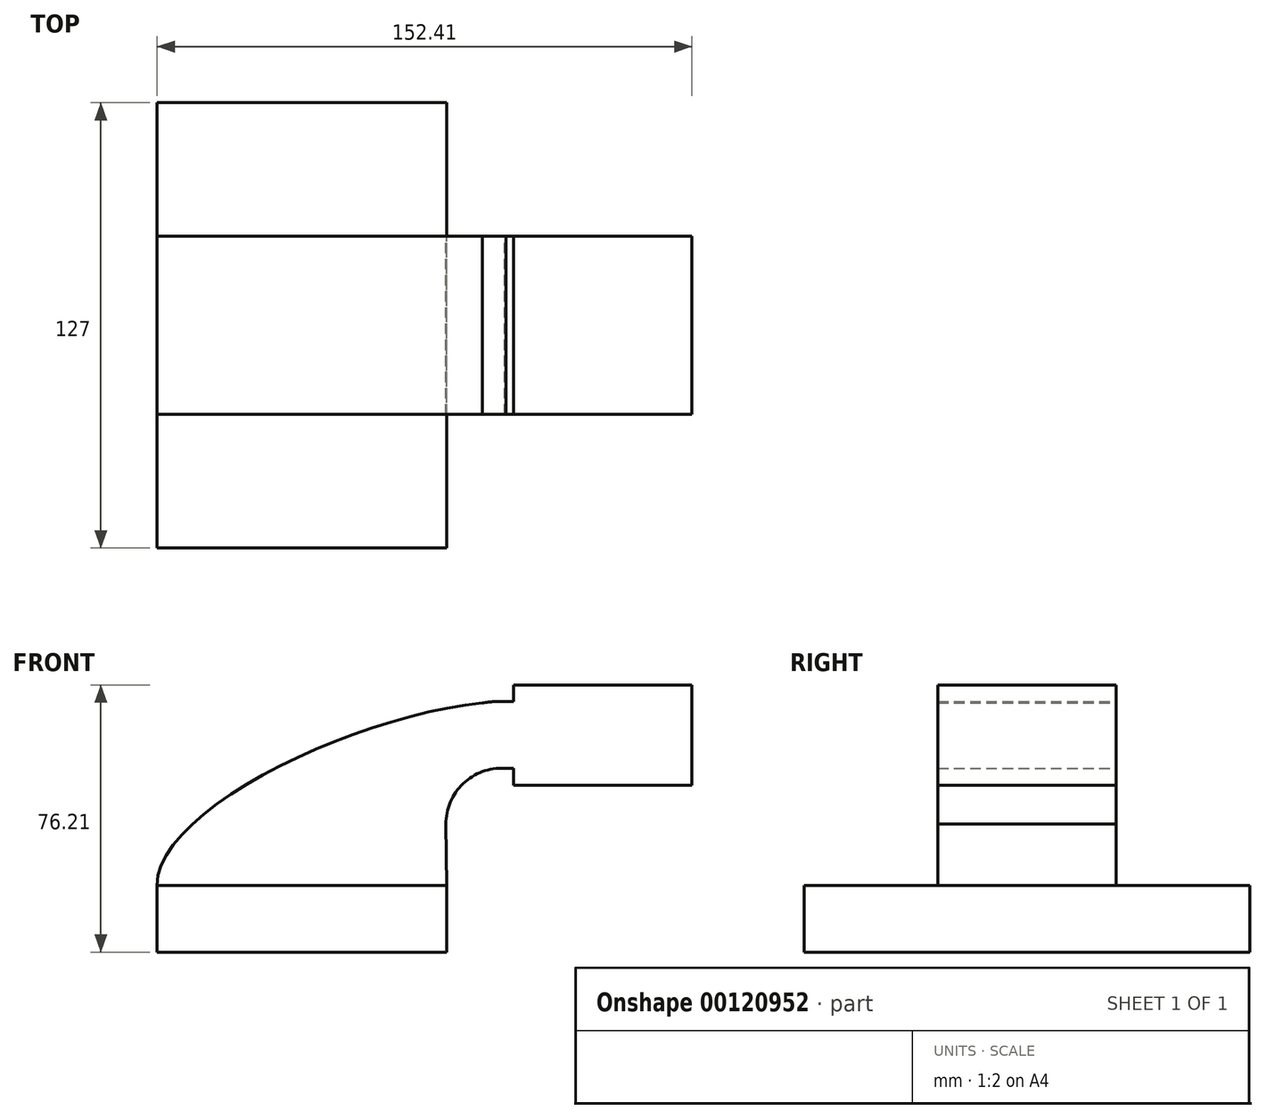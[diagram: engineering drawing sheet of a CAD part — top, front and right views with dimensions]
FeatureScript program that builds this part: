
annotation { "Feature Type Name" : "Feature", "Feature Type Description" : "" }
export const myFeature = defineFeature(function(context is Context, id is Id, definition is map)
    precondition{}
    {
        {
            var Q0;
            Q0=qCreatedBy(makeId("Front.planeOp"),FACE);
            var sketch = newSketch(context, id + "F0", { "sketchPlane" : qUnion([Q0])});
            skArc(sketch, "E0", {"start": v(41.01, 26.95) * mm, "mid": v(45.94, 38.52) * mm, "end": v(57.75, 42.88) * mm});
            skLineSegment(sketch, "E1.bottom", {"start": v(-41.28, -9.53) * mm, "end": v(41.27, -9.53) * mm});
            skLineSegment(sketch, "E1.top", {"start": v(-41.28, 9.53) * mm, "end": v(41.27, 9.53) * mm});
            skLineSegment(sketch, "E1.left", {"start": v(-41.28, -9.53) * mm, "end": v(-41.28, 9.53) * mm});
            skLineSegment(sketch, "E1.right", {"start": v(41.27, -9.53) * mm, "end": v(41.27, 9.53) * mm});
            skPoint(sketch, "E1.middle", {"position": v(0, 0) * mm});
            skLineSegment(sketch, "E2.bottom", {"start": v(60.32, 38.1) * mm, "end": v(111.13, 38.1) * mm});
            skLineSegment(sketch, "E2.top", {"start": v(60.32, 66.67) * mm, "end": v(111.13, 66.67) * mm});
            skLineSegment(sketch, "E2.left", {"start": v(60.32, 38.1) * mm, "end": v(60.32, 66.67) * mm});
            skLineSegment(sketch, "E2.right", {"start": v(111.13, 38.1) * mm, "end": v(111.13, 66.67) * mm});
            skPoint(sketch, "E2.middle", {"position": v(85.72, 52.39) * mm});
            skLineSegment(sketch, "E3", {"start": v(41.28, 9.52) * mm, "end": v(41.01, 26.95) * mm});
            skArc(sketch, "E4.1", {"start": v(21.96, 26.73) * mm, "mid": v(32.54, 52.07) * mm, "end": v(58.16, 61.93) * mm});
            skLineSegment(sketch, "E4.2", {"start": v(22.23, 9.24) * mm, "end": v(21.96, 26.73) * mm});
            skLineSegment(sketch, "E5", {"start": v(57.75, 42.88) * mm, "end": v(85.72, 42.88) * mm});
            skLineSegment(sketch, "E6", {"start": v(58.16, 61.93) * mm, "end": v(85.72, 61.93) * mm});
            skLineSegment(sketch, "E7", {"start": v(85.72, 66.67) * mm, "end": v(85.72, 38.1) * mm});
            skFitSpline(sketch, "E8", {"points": [v(-41.28, 9.53) * mm, v(58.16, 61.93) * mm], "startDerivative": vector(-0.85, 68.54) * mm, "endDerivative": vector(108.5, 1.9) * mm});
            skSolve(sketch);
        }
        {
            var Q0;
            Q0=makeQuery(id+"F0.imprint","IMPRINT",FACE,{"disambiguationData":[TD([[makeQuery(id+"F0.imprint","IMPRINT",EDGE,{"derivedFrom":sQuery(id+"F0.wireOp",EDGE,"E1.bottom")}),1.0]])]});
            extrude(context, id + "F1", {"entities" : qUnion([Q0]), "endBound" : BoundingType.SYMMETRIC, "depth" : 127 * mm});
        }
        {
            var Q0;
            {var subQ0=sQuery(id+"F0.wireOp",EDGE,"E8");var subQ1=sQuery(id+"F0.wireOp",EDGE,"E4.1");var subQ3=makeQuery(id+"F0.imprint","INTERSECT",VERTEX,{"derivedFrom":[subQ1,subQ0]});Q0=makeQuery(id+"F0.imprint","IMPRINT",FACE,{"disambiguationData":[TD([[makeQuery(id+"F0.imprint","IMPRINT",EDGE,{"disambiguationData":[TD([[subQ3,-1.0]])],"derivedFrom":subQ1}),-1.0]])]});}
            var Q1;
            Q1=makeQuery(id+"F0.imprint","IMPRINT",FACE,{"disambiguationData":[TD([[makeQuery(id+"F0.imprint","IMPRINT",EDGE,{"derivedFrom":sQuery(id+"F0.wireOp",EDGE,"E1.bottom")}),1.0]])]});
            var Q2;
            {var subQ2=sQuery(id+"F0.wireOp",EDGE,"E0");Q2=makeQuery(id+"F0.imprint","IMPRINT",FACE,{"disambiguationData":[TD([[makeQuery(id+"F0.imprint","IMPRINT",EDGE,{"derivedFrom":subQ2}),1.0]])]});}
            var Q3;
            {var subQ2=sQuery(id+"F0.wireOp",EDGE,"E0");Q3=makeQuery(id+"F0.imprint","IMPRINT",FACE,{"disambiguationData":[TD([[makeQuery(id+"F0.imprint","IMPRINT",EDGE,{"derivedFrom":subQ2}),1.0]])]});}
            var Q4;
            {var subQ0=sQuery(id+"F0.wireOp",EDGE,"E5");var subQ1=sQuery(id+"F0.wireOp",EDGE,"E2.left");var subQ2=makeQuery(id+"F0.imprint","INTERSECT",VERTEX,{"derivedFrom":[subQ1,subQ0]});Q4=makeQuery(id+"F0.imprint","IMPRINT",FACE,{"disambiguationData":[TD([[makeQuery(id+"F0.imprint","IMPRINT",EDGE,{"disambiguationData":[TD([[subQ2,-1.0]])],"derivedFrom":subQ1}),-1.0]])]});}
            var Q5;
            {var subQ0=sQuery(id+"F0.wireOp",EDGE,"E2.left");var subQ1=sQuery(id+"F0.wireOp",EDGE,"E2.bottom");var subQ2=makeQuery(id+"F0.imprint","INTERSECT",VERTEX,{"derivedFrom":[subQ1,subQ0]});Q5=makeQuery(id+"F0.imprint","IMPRINT",FACE,{"disambiguationData":[TD([[makeQuery(id+"F0.imprint","IMPRINT",EDGE,{"disambiguationData":[TD([[subQ2,-1.0]])],"derivedFrom":subQ1}),1.0]])]});}
            var Q6;
            {var subQ0=sQuery(id+"F0.wireOp",EDGE,"E2.right");Q6=makeQuery(id+"F0.imprint","IMPRINT",FACE,{"disambiguationData":[TD([[makeQuery(id+"F0.imprint","IMPRINT",EDGE,{"derivedFrom":subQ0}),1.0]])]});}
            var Q7;
            {var subQ0=sQuery(id+"F0.wireOp",EDGE,"E2.left");var subQ1=sQuery(id+"F0.wireOp",EDGE,"E2.top");var subQ2=makeQuery(id+"F0.imprint","INTERSECT",VERTEX,{"derivedFrom":[subQ1,subQ0]});Q7=makeQuery(id+"F0.imprint","IMPRINT",FACE,{"disambiguationData":[TD([[makeQuery(id+"F0.imprint","IMPRINT",EDGE,{"disambiguationData":[TD([[subQ2,-1.0]])],"derivedFrom":subQ1}),-1.0]])]});}
            extrude(context, id + "F2", {"entities" : qUnion([Q0, Q1, Q2, Q3, Q4, Q5, Q6, Q7]), "operationType" : NewBodyOperationType.ADD, "endBound" : BoundingType.SYMMETRIC, "depth" : 50.8 * mm});
        }
        {
            var Q0;
            Q0 = qSketchRegion(id + "F0", true);
            extrude(context, id + "F3", {"entities" : qUnion([Q0]), "operationType" : NewBodyOperationType.ADD, "endBound" : BoundingType.SYMMETRIC, "depth" : 50.8 * mm});
        }
    });
